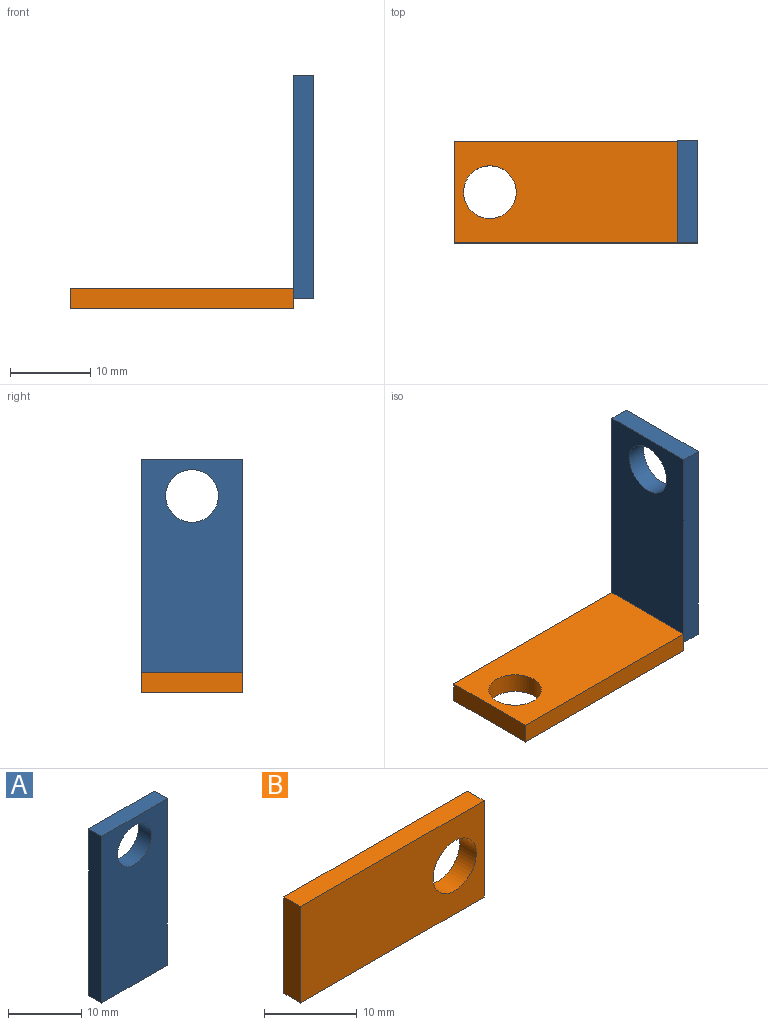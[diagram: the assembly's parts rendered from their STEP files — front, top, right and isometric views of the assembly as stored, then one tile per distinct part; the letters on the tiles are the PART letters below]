
ASSEMBLY  parts=2 mates=1
PART A: 7 faces, bbox 12.7x2.5x27.9 mm
  f0: plane 12.7x2.54mm, normal (0,0,1), area 32.3mm2, adj f1,f4,f5,f6
  f1: plane 27.94x2.54mm, normal (-1,0,0), area 71mm2, adj f0,f2,f5,f6
  f2: plane 12.7x2.54mm, normal (0,0,-1), area 32.3mm2, adj f1,f4,f5,f6
  f3: cylinder r=3.29mm len=6.58mm, axis (0,1,0), area 52.5mm2, adj f5,f6
  f4: plane 27.94x2.54mm, normal (1,0,0), area 71mm2, adj f0,f2,f5,f6
  f5: plane 27.94x12.7mm, normal (0,-1,0), area 320.8mm2, adj f0,f1,f2,f3,f4
  f6: plane 27.94x12.7mm, normal (0,1,0), area 320.8mm2, adj f0,f1,f2,f3,f4
PART B: 7 faces, bbox 27.9x2.5x12.7 mm
  f0: plane 27.94x2.54mm, normal (0,0,1), area 71mm2, adj f1,f3,f5,f6
  f1: plane 12.7x2.54mm, normal (-1,0,0), area 32.3mm2, adj f0,f2,f5,f6
  f2: plane 27.94x2.54mm, normal (0,0,-1), area 71mm2, adj f1,f3,f5,f6
  f3: plane 12.7x2.54mm, normal (1,0,0), area 32.3mm2, adj f0,f2,f5,f6
  f4: cylinder r=3.29mm len=6.58mm, axis (0,1,0), area 52.5mm2, adj f5,f6
  f5: plane 27.94x12.7mm, normal (0,-1,0), area 320.8mm2, adj f0,f1,f2,f3,f4
  f6: plane 27.94x12.7mm, normal (0,1,0), area 320.8mm2, adj f0,f1,f2,f3,f4
PLACE A rot(axis=(0,0,1),90deg) t=(9.23,36.32,-15.64)mm
PLACE B rot(axis=(0,-0.71,0.71),180deg) t=(-24.51,6.47,-7.32)mm
MATE fastened A.f6 <-> B.f1  axis (-1,0,0) through (9.23,-0.99,-6.05)mm
